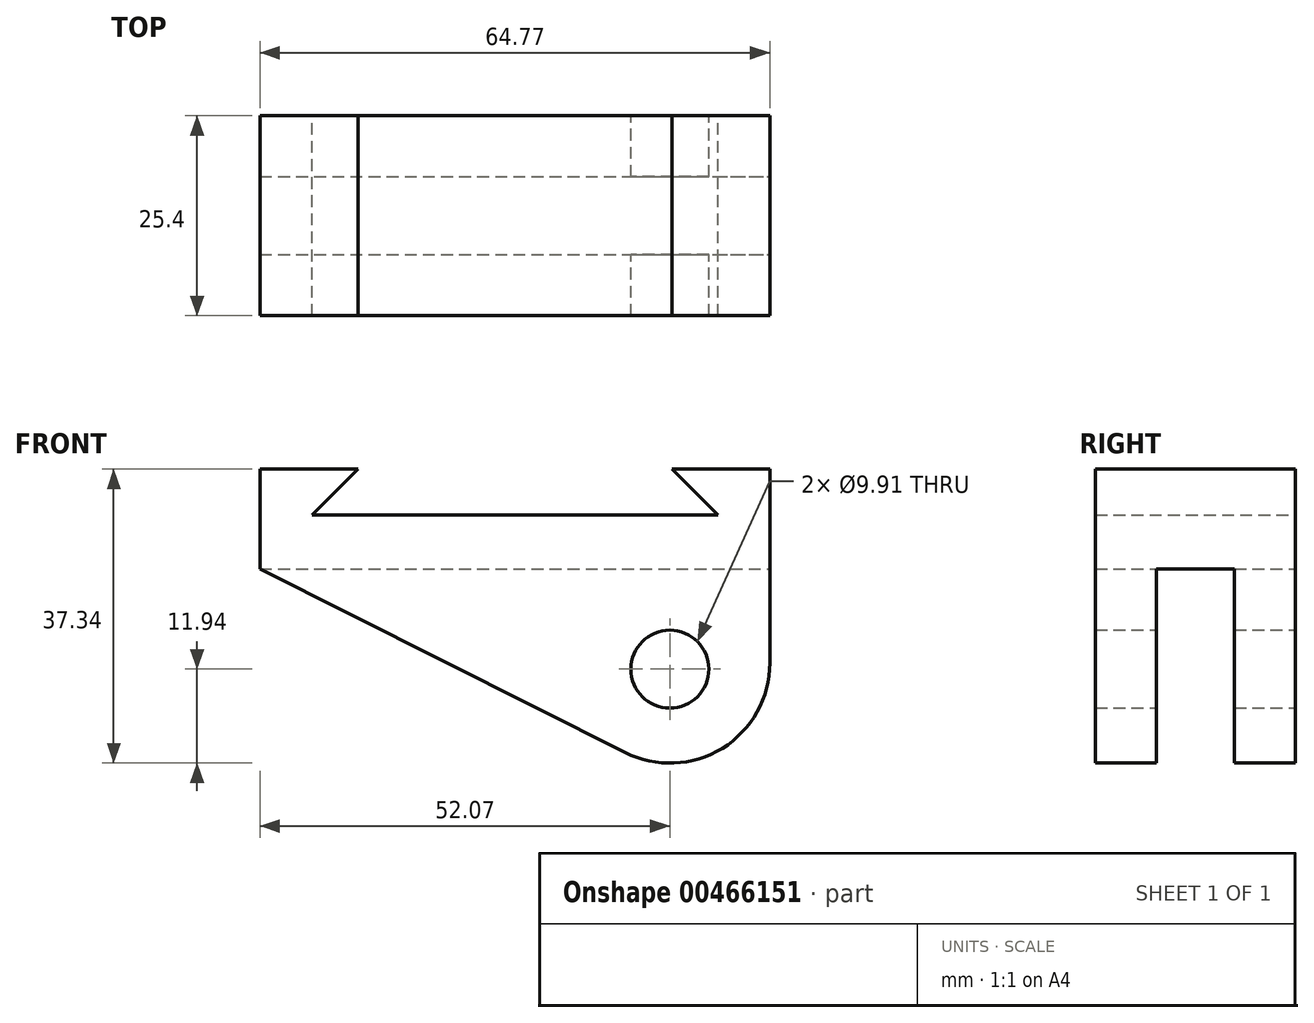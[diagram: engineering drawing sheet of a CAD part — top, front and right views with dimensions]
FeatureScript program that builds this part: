
annotation { "Feature Type Name" : "Feature", "Feature Type Description" : "" }
export const myFeature = defineFeature(function(context is Context, id is Id, definition is map)
    precondition{}
    {
        {
            var Q0;
            Q0=qCreatedBy(makeId("Front.planeOp"),FACE);
            var sketch = newSketch(context, id + "F0", { "sketchPlane" : qUnion([Q0])});
            skLineSegment(sketch, "E0.bottom", {"start": v(-52.07, 12.7) * mm, "end": v(-39.62, 12.7) * mm});
            skLineSegment(sketch, "E0.top", {"start": v(-52.07, 0) * mm, "end": v(12.7, 0) * mm, "construction": true});
            skLineSegment(sketch, "E0.left", {"start": v(-52.07, 12.7) * mm, "end": v(-52.07, 0) * mm});
            skLineSegment(sketch, "E0.right", {"start": v(12.7, 12.7) * mm, "end": v(12.7, 0) * mm});
            skLineSegment(sketch, "E1", {"start": v(-39.62, 12.7) * mm, "end": v(-45.47, 6.86) * mm});
            skLineSegment(sketch, "E2", {"start": v(-45.47, 6.86) * mm, "end": v(-52.07, 6.86) * mm, "construction": true});
            skLineSegment(sketch, "E3", {"start": v(0.25, 12.7) * mm, "end": v(6.1, 6.86) * mm});
            skLineSegment(sketch, "E4", {"start": v(6.1, 6.86) * mm, "end": v(12.7, 6.86) * mm, "construction": true});
            skLineSegment(sketch, "E5.trimOffspring", {"start": v(0.25, 12.7) * mm, "end": v(12.7, 12.7) * mm});
            skLineSegment(sketch, "E6", {"start": v(-45.47, 6.86) * mm, "end": v(6.1, 6.86) * mm});
            skLineSegment(sketch, "E7", {"start": v(-52.07, 0) * mm, "end": v(-5.7, -23.29) * mm});
            skLineSegment(sketch, "E8", {"start": v(12.7, 0) * mm, "end": v(12.7, -11.94) * mm});
            skArc(sketch, "E9", {"start": v(-5.7, -23.29) * mm, "mid": v(6.67, -22.75) * mm, "end": v(12.7, -11.94) * mm});
            skLineSegment(sketch, "E10", {"start": v(0, 0) * mm, "end": v(0, -24.64) * mm, "construction": true});
            skCircle(sketch, "E11", {"center": v(0, -12.7) * mm, "radius": 4.95 * mm});
            skSolve(sketch);
        }
        {
            var Q0;
            Q0 = qSketchRegion(id + "F0", true);
            extrude(context, id + "F1", {"entities" : qUnion([Q0]), "endBound" : BoundingType.SYMMETRIC, "depth" : 25.4 * mm});
        }
        {
            var Q0;
            Q0=qCreatedBy(makeId("Top.planeOp"),FACE);
            var sketch = newSketch(context, id + "F2", { "sketchPlane" : qUnion([Q0])});
            skLineSegment(sketch, "E12.bottom", {"start": v(-52.07, 4.95) * mm, "end": v(12.7, 4.95) * mm});
            skLineSegment(sketch, "E12.top", {"start": v(-52.07, -4.95) * mm, "end": v(12.7, -4.95) * mm});
            skLineSegment(sketch, "E12.left", {"start": v(-52.07, 4.95) * mm, "end": v(-52.07, -4.95) * mm});
            skLineSegment(sketch, "E12.right", {"start": v(12.7, 4.95) * mm, "end": v(12.7, -4.95) * mm});
            skLineSegment(sketch, "E13", {"start": v(-52.07, 4.95) * mm, "end": v(12.7, -4.95) * mm, "construction": true});
            skPoint(sketch, "E14", {"position": v(19.61, -17.6) * mm});
            skPoint(sketch, "E15", {"position": v(-19.69, 0) * mm});
            skSolve(sketch);
        }
        {
            var Q0;
            Q0 = qSketchRegion(id + "F2", true);
            extrude(context, id + "F3", {"entities" : qUnion([Q0]), "operationType" : NewBodyOperationType.REMOVE, "endBound" : BoundingType.THROUGH_ALL, "oppositeDirection" : true, "depth" : 25.4 * mm});
        }
    });
